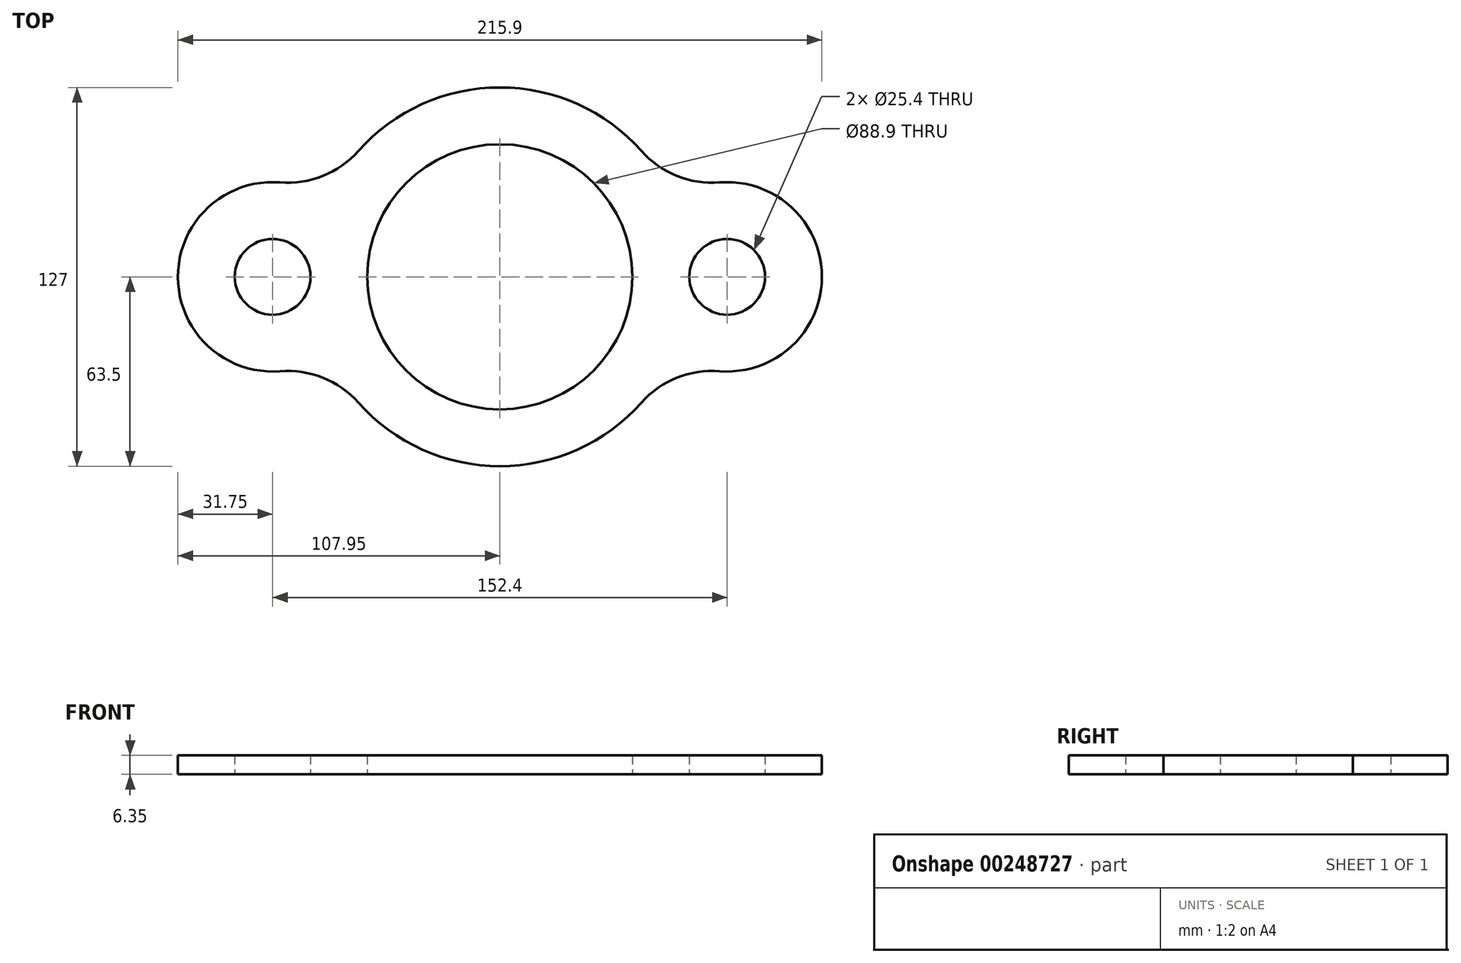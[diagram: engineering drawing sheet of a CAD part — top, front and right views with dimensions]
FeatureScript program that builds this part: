
annotation { "Feature Type Name" : "Feature", "Feature Type Description" : "" }
export const myFeature = defineFeature(function(context is Context, id is Id, definition is map)
    precondition{}
    {
        {
            var Q0;
            Q0=qCreatedBy(makeId("Top.planeOp"),FACE);
            var sketch = newSketch(context, id + "F0", { "sketchPlane" : qUnion([Q0])});
            skArc(sketch, "E0", {"start": v(-47.45, -42.2) * mm, "mid": v(0, -63.5) * mm, "end": v(47.45, -42.2) * mm});
            skCircle(sketch, "E1", {"center": v(0, 0) * mm, "radius": 44.45 * mm});
            skArc(sketch, "E2", {"start": v(73.69, -31.65) * mm, "mid": v(107.95, 0) * mm, "end": v(73.69, 31.65) * mm});
            skCircle(sketch, "E3", {"center": v(76.2, 0) * mm, "radius": 12.7 * mm});
            skArc(sketch, "E4", {"start": v(-73.69, 31.65) * mm, "mid": v(-107.95, 0) * mm, "end": v(-73.69, -31.65) * mm});
            skCircle(sketch, "E5", {"center": v(-76.2, 0) * mm, "radius": 12.7 * mm});
            skPoint(sketch, "E6", {"position": v(23.4, -59.03) * mm});
            skArc(sketch, "E7.trimOffspring", {"start": v(47.45, 42.2) * mm, "mid": v(0, 63.5) * mm, "end": v(-47.45, 42.2) * mm});
            skPoint(sketch, "E8.visualSharp", {"position": v(-57.94, 25.98) * mm});
            skArc(sketch, "E8.filletArc", {"start": v(-73.69, 31.65) * mm, "mid": v(-59.33, 33.84) * mm, "end": v(-47.45, 42.2) * mm});
            skPoint(sketch, "E9.visualSharp", {"position": v(-57.94, -25.98) * mm});
            skArc(sketch, "E9.filletArc", {"start": v(-47.45, -42.2) * mm, "mid": v(-59.33, -33.84) * mm, "end": v(-73.69, -31.65) * mm});
            skPoint(sketch, "E10.visualSharp", {"position": v(57.94, -25.98) * mm});
            skArc(sketch, "E10.filletArc", {"start": v(73.69, -31.65) * mm, "mid": v(59.33, -33.84) * mm, "end": v(47.45, -42.2) * mm});
            skPoint(sketch, "E11.visualSharp", {"position": v(57.94, 25.98) * mm});
            skArc(sketch, "E11.filletArc", {"start": v(47.45, 42.2) * mm, "mid": v(59.33, 33.84) * mm, "end": v(73.69, 31.65) * mm});
            skSolve(sketch);
        }
        {
            var Q0;
            Q0=makeQuery(id+"F0.imprint","IMPRINT",FACE,{"disambiguationData":[TD([[makeQuery(id+"F0.imprint","IMPRINT",EDGE,{"derivedFrom":sQuery(id+"F0.wireOp",EDGE,"E0")}),1.0]])]});
            extrude(context, id + "F1", {"entities" : qUnion([Q0]), "depth" : 6.35 * mm});
        }
    });
